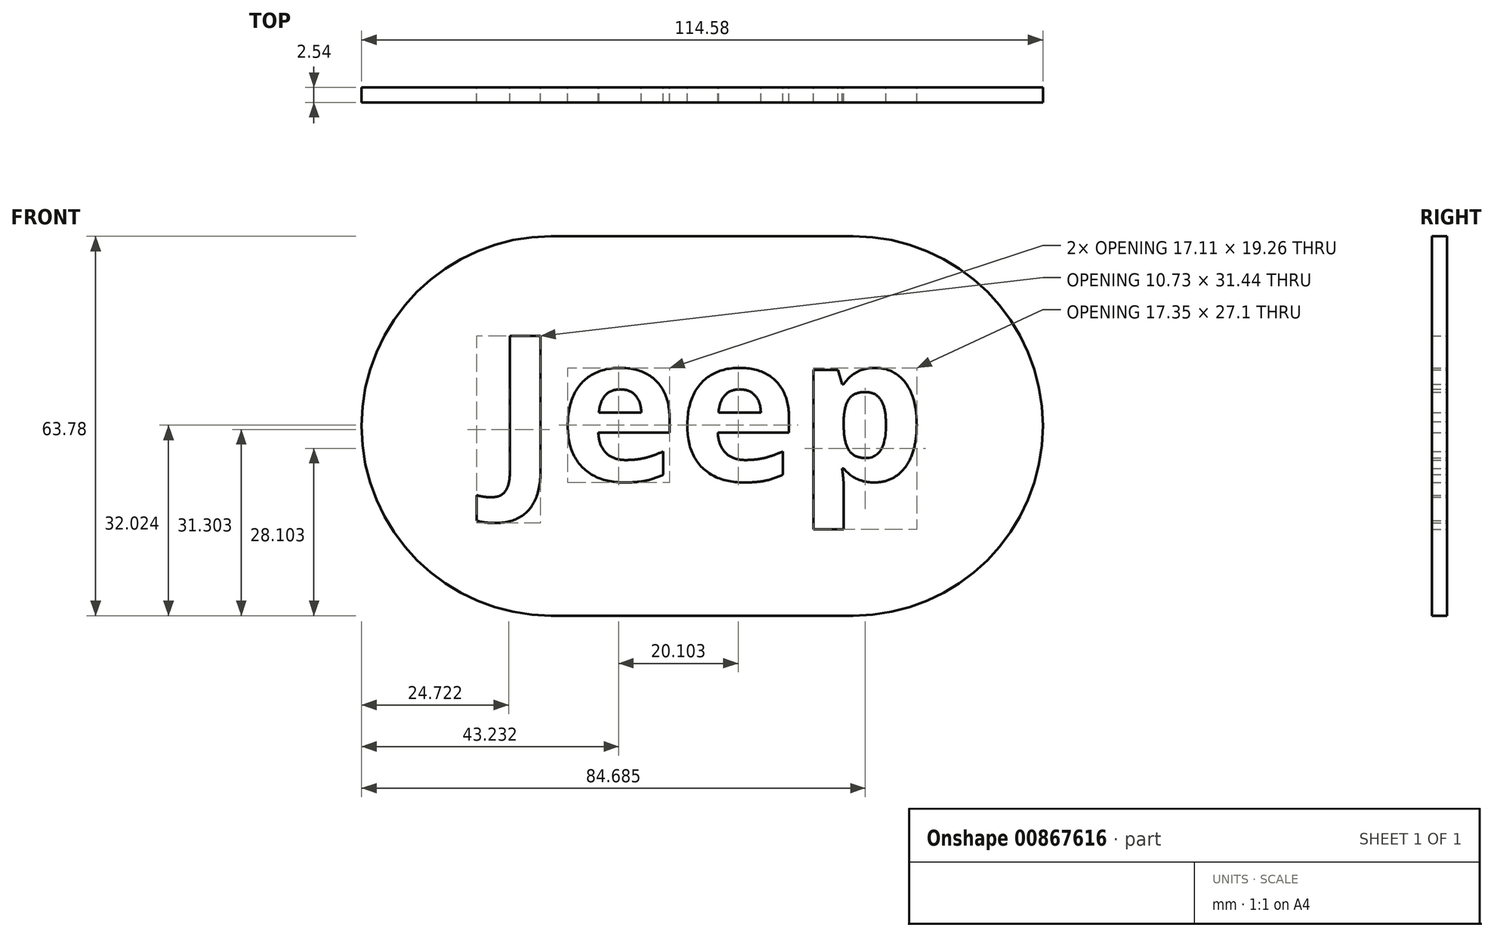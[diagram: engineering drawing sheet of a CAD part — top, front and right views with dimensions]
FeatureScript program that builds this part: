
annotation { "Feature Type Name" : "Feature", "Feature Type Description" : "" }
export const myFeature = defineFeature(function(context is Context, id is Id, definition is map)
    precondition{}
    {
        {
            var Q0;
            Q0=qCreatedBy(makeId("Front.planeOp"),FACE);
            var sketch = newSketch(context, id + "F0", { "sketchPlane" : qUnion([Q0])});
            skLineSegment(sketch, "E0.bottom", {"start": v(15.13, 28.04) * mm, "end": v(65.93, 28.04) * mm});
            skLineSegment(sketch, "E0.top", {"start": v(15.13, -22.76) * mm, "end": v(65.93, -22.76) * mm});
            skLineSegment(sketch, "E0.right", {"start": v(65.93, 28.04) * mm, "end": v(65.93, 28.04) * mm});
            skArc(sketch, "E1", {"start": v(15.13, 28.04) * mm, "mid": v(-10.27, 2.64) * mm, "end": v(15.13, -22.76) * mm});
            skArc(sketch, "E2", {"start": v(65.93, -22.76) * mm, "mid": v(91.33, 2.64) * mm, "end": v(65.93, 28.04) * mm});
            skLineSegment(sketch, "E3.trimOffspring", {"start": v(65.93, -22.76) * mm, "end": v(65.93, -22.76) * mm});
            skPoint(sketch, "E4.orphan", {"position": v(15.13, -22.76) * mm});
            skPoint(sketch, "E5.orphan", {"position": v(15.13, 28.04) * mm});
            skPoint(sketch, "E6.orphan", {"position": v(-12.74, 28.04) * mm});
            skPoint(sketch, "E7.end.orphan", {"position": v(-12.74, -22.76) * mm});
            skPoint(sketch, "E7.start.orphan", {"position": v(-12.74, 2.64) * mm});
            skPoint(sketch, "E8.trimOffspring.end.orphan", {"position": v(-10.27, 2.64) * mm});
            skPoint(sketch, "E9.start.orphan", {"position": v(91.33, 2.64) * mm});
            skText(sketch, "E10", { "text": "Jeep", "fontName": "OpenSans-Bold.ttf"});
            skLineSegment(sketch, "E11", {"start": v(15.13, -29.77) * mm, "end": v(65.93, -29.77) * mm});
            skLineSegment(sketch, "E12", {"start": v(15.13, 34) * mm, "end": v(65.93, 34) * mm});
            skArc(sketch, "E13", {"start": v(15.13, 34) * mm, "mid": v(-16.76, 2.12) * mm, "end": v(15.13, -29.77) * mm});
            skArc(sketch, "E14", {"start": v(65.93, 34) * mm, "mid": v(97.82, 2.12) * mm, "end": v(65.93, -29.77) * mm});
            const initialGuessF0  = {"E10": [0.00512, -0.00704, 1, 0, 0.0245]};
            skSetInitialGuess(sketch, initialGuessF0);
            skSolve(sketch);
        }
        {
            var Q0;
            Q0=makeQuery(id+"F0.imprint","IMPRINT",FACE,{"disambiguationData":[TD([[makeQuery(id+"F0.imprint","IMPRINT",EDGE,{"derivedFrom":sQuery(id+"F0.wireOp",EDGE,"E0.bottom")}),1.0]])]});
            var Q1;
            Q1=makeQuery(id+"F0.imprint","IMPRINT",FACE,{"disambiguationData":[TD([[makeQuery(id+"F0.imprint","IMPRINT",EDGE,{"derivedFrom":sQuery(id+"F0.wireOp",EDGE,"E0.bottom")}),-1.0]])]});
            extrude(context, id + "F1", {"entities" : qUnion([Q0, Q1]), "depth" : 2.54 * mm, "offsetDistance" : 25.4 * mm});
        }
        {
            var Q0;
            Q0=makeQuery(id+"F0.imprint","IMPRINT",FACE,{"disambiguationData":[TD([[makeQuery(id+"F0.imprint","IMPRINT",EDGE,{"derivedFrom":sQuery(id+"F0.wireOp",EDGE,"E10.sketch_text.stroke-65")}),1.0]])]});
            var Q1;
            Q1=makeQuery(id+"F0.imprint","IMPRINT",FACE,{"disambiguationData":[TD([[makeQuery(id+"F0.imprint","IMPRINT",EDGE,{"derivedFrom":sQuery(id+"F0.wireOp",EDGE,"E10.sketch_text.stroke-10")}),1.0]])]});
            var Q2;
            Q2=makeQuery(id+"F0.imprint","IMPRINT",FACE,{"disambiguationData":[TD([[makeQuery(id+"F0.imprint","IMPRINT",EDGE,{"derivedFrom":sQuery(id+"F0.wireOp",EDGE,"E10.sketch_text.stroke-30")}),1.0]])]});
            extrude(context, id + "F2", {"entities" : qUnion([Q0, Q1, Q2]), "depth" : 2.54 * mm, "offsetDistance" : 25.4 * mm});
        }
    });
